# Revit family: REVIT-TR-250-3000
name_source: partatom
category: Mechanical Equipment
revit_build: Autodesk Revit 2017 (Build: 20190507_1515(x64)
units: mm (PartAtom-declared; Revit-internal decimal feet)

## family parameters
Always vertical = Yes
Cut with Voids When Loaded = No
Part Type = Normal
Room Calculation Point = No
Round Connector Dimension = Use Radius
Shared = No
Work Plane-Based = No

## types (14) — shared parameters
Assembly Code = D3040400
Controll Access Angle = 45.00°
Description = Storage Tanks for Hot Water
Disclaimer = This rendering is for building modeling purposes only. Submittal/catalog is still the contract document. PVI reserves the right to change design and specification without notice.
Drain Angle = 90.00°
Manufacturer = PVI Industries, LLC
Manway Access Radius = 6 1/2"
Relief NPT = 1"
Relief Radius = 1/2"
URL = www.pvi.com

## per-type parameters (varying)
- L 250A-TR: Cold Inlet Extension=24"; Cold Inlet Height=17 7/8"; Cold Inlet NPT=2"; Cold Inlet Radius=1"; Drain Extension=26 7/8"; Drain Height=3 1/2"; Drain NPT=1"; Drain Radius=1/2"; Flat Side Distance=45 255/256"; From Heater Extension=24"; From Heater Height=19"; From Heater NPT=2"; From Heater Radius=1"; Gallons Storage=250 CF; Height to Upper Drain=25 9/64"; Hot Outlet NPT=2"; Hot Outlet Radius=1"; Manway Access Extension=26"; Relief Angle=45.00°; Relief Extension=24"; Relief Height=46 1/4"; Skid Length=46"; Skid Spacing=27"; SkidWidthBetweenCenters=31"; To Heater Extension=24"; To Heater Height=27"; To Heater NPT=2"; To Heater Radius=1"; Unit Diameter=46"; Unit Height=63"; Unit Radius=23"; Weight=945
- L 300A-TR: Cold Inlet Extension=24"; Cold Inlet Height=17 7/8"; Cold Inlet NPT=2"; Cold Inlet Radius=1"; Drain Extension=26 7/8"; Drain Height=3 1/2"; Drain NPT=1"; Drain Radius=1/2"; Flat Side Distance=45 255/256"; From Heater Extension=24"; From Heater Height=19"; From Heater NPT=2"; From Heater Radius=1"; Gallons Storage=300 CF; Height to Upper Drain=25 9/64"; Hot Outlet NPT=2"; Hot Outlet Radius=1"; Manway Access Extension=26"; Relief Angle=45.00°; Relief Extension=24"; Relief Height=58 1/4"; Skid Length=46"; Skid Spacing=27"; SkidWidthBetweenCenters=31"; To Heater Extension=24"; To Heater Height=27"; To Heater NPT=2"; To Heater Radius=1"; Unit Diameter=46"; Unit Height=75"; Unit Radius=23"; Weight=1010
- L 400A-TR: Cold Inlet Extension=24"; Cold Inlet Height=17 7/8"; Cold Inlet NPT=2"; Cold Inlet Radius=1"; Drain Extension=26 7/8"; Drain Height=3 1/2"; Drain NPT=1"; Drain Radius=1/2"; Flat Side Distance=45 255/256"; From Heater Extension=24"; From Heater Height=19"; From Heater NPT=2"; From Heater Radius=1"; Gallons Storage=400 CF; Height to Upper Drain=25 9/64"; Hot Outlet NPT=2"; Hot Outlet Radius=1"; Manway Access Extension=26"; Relief Angle=45.00°; Relief Extension=24"; Relief Height=70 1/4"; Skid Length=46"; Skid Spacing=27"; SkidWidthBetweenCenters=31"; To Heater Extension=24"; To Heater Height=27"; To Heater NPT=2"; To Heater Radius=1"; Unit Diameter=46"; Unit Height=87"; Unit Radius=23"; Weight=1070
- L 500A-TR: Cold Inlet Extension=29"; Cold Inlet Height=19 3/4"; Cold Inlet NPT=3"; Cold Inlet Radius=1 1/2"; Drain Extension=31 7/8"; Drain Height=3 3/4"; Drain NPT=1 1/2"; Drain Radius=3/4"; Flat Side Distance=55 255/256"; From Heater Extension=29"; From Heater Height=24"; From Heater NPT=3"; From Heater Radius=1 1/2"; Gallons Storage=500 CF; Height to Upper Drain=25 9/64"; Hot Outlet NPT=3"; Hot Outlet Radius=1 1/2"; Manway Access Extension=31"; Relief Angle=38.00°; Relief Extension=29"; Relief Height=59 1/2"; Skid Length=54 1/2"; Skid Spacing=27"; SkidWidthBetweenCenters=31"; To Heater Extension=29"; To Heater Height=32"; To Heater NPT=3"; To Heater Radius=1 1/2"; Unit Diameter=56"; Unit Height=78"; Unit Radius=28"; Weight=1415
- L 600A-TR: Cold Inlet Extension=29"; Cold Inlet Height=19 3/4"; Cold Inlet NPT=3"; Cold Inlet Radius=1 1/2"; Drain Extension=31 7/8"; Drain Height=3 3/4"; Drain NPT=1 1/2"; Drain Radius=3/4"; Flat Side Distance=55 255/256"; From Heater Extension=29"; From Heater Height=24"; From Heater NPT=3"; From Heater Radius=1 1/2"; Gallons Storage=600 CF; Height to Upper Drain=25 9/64"; Hot Outlet NPT=3"; Hot Outlet Radius=1 1/2"; Manway Access Extension=31"; Relief Angle=38.00°; Relief Extension=29"; Relief Height=71 1/2"; Skid Length=54 1/2"; Skid Spacing=27"; SkidWidthBetweenCenters=31"; To Heater Extension=29"; To Heater Height=32"; To Heater NPT=3"; To Heater Radius=1 1/2"; Unit Diameter=56"; Unit Height=90"; Unit Radius=28"; Weight=1605
- L 750A-TR: Cold Inlet Extension=34 1/2"; Cold Inlet Height=22 1/2"; Cold Inlet NPT=3"; Cold Inlet Radius=1 1/2"; Drain Extension=37 3/8"; Drain Height=3 3/4"; Drain NPT=1 1/2"; Drain Radius=3/4"; Flat Side Distance=66 255/256"; From Heater Extension=34 1/2"; From Heater Height=24"; From Heater NPT=3"; From Heater Radius=1 1/2"; Gallons Storage=750 CF; Height to Upper Drain=25 9/64"; Hot Outlet NPT=3"; Hot Outlet Radius=1 1/2"; Manway Access Extension=36 1/2"; Relief Angle=45.00°; Relief Extension=34 1/2"; Relief Height=62 1/4"; Skid Length=68"; Skid Spacing=36"; SkidWidthBetweenCenters=40"; To Heater Extension=34 1/2"; To Heater Height=32"; To Heater NPT=3"; To Heater Radius=1 1/2"; Unit Diameter=67"; Unit Height=83"; Unit Radius=33 1/2"; Weight=1770
- L 900A-TR: Cold Inlet Extension=34 1/2"; Cold Inlet Height=22 1/2"; Cold Inlet NPT=3"; Cold Inlet Radius=1 1/2"; Drain Extension=37 3/8"; Drain Height=3 3/4"; Drain NPT=1 1/2"; Drain Radius=3/4"; Flat Side Distance=66 255/256"; From Heater Extension=34 1/2"; From Heater Height=24"; From Heater NPT=3"; From Heater Radius=1 1/2"; Gallons Storage=900 CF; Height to Upper Drain=25 9/64"; Hot Outlet NPT=3"; Hot Outlet Radius=1 1/2"; Manway Access Extension=36 1/2"; Relief Angle=45.00°; Relief Extension=34 1/2"; Relief Height=74 1/4"; Skid Length=68"; Skid Spacing=36"; SkidWidthBetweenCenters=40"; To Heater Extension=34 1/2"; To Heater Height=32"; To Heater NPT=3"; To Heater Radius=1 1/2"; Unit Diameter=67"; Unit Height=95"; Unit Radius=33 1/2"; Weight=1990
- L 1000A-TR: Cold Inlet Extension=34 1/2"; Cold Inlet Height=22 1/2"; Cold Inlet NPT=3"; Cold Inlet Radius=1 1/2"; Drain Extension=37 3/8"; Drain Height=3 3/4"; Drain NPT=1 1/2"; Drain Radius=3/4"; Flat Side Distance=66 255/256"; From Heater Extension=34 1/2"; From Heater Height=24"; From Heater NPT=3"; From Heater Radius=1 1/2"; Gallons Storage=1000 CF; Height to Upper Drain=25 9/64"; Hot Outlet NPT=3"; Hot Outlet Radius=1 1/2"; Manway Access Extension=36 1/2"; Relief Angle=45.00°; Relief Extension=34 1/2"; Relief Height=86 1/4"; Skid Length=68"; Skid Spacing=36"; SkidWidthBetweenCenters=40"; To Heater Extension=34 1/2"; To Heater Height=32"; To Heater NPT=3"; To Heater Radius=1 1/2"; Unit Diameter=67"; Unit Height=107"; Unit Radius=33 1/2"; Weight=2210
- L 1250A-TR: Cold Inlet Extension=38 1/2"; Cold Inlet Height=22 1/2"; Cold Inlet NPT=3"; Cold Inlet Radius=1 1/2"; Drain Extension=41 3/8"; Drain Height=3 3/4"; Drain NPT=1 1/2"; Drain Radius=3/4"; Flat Side Distance=74 255/256"; From Heater Extension=38 1/2"; From Heater Height=23"; From Heater NPT=3"; From Heater Radius=1 1/2"; Gallons Storage=1250 CF; Height to Upper Drain=25"; Hot Outlet NPT=3"; Hot Outlet Radius=1 1/2"; Manway Access Extension=40 1/2"; Relief Angle=67.50°; Relief Extension=38 1/2"; Relief Height=76 1/4"; Skid Length=75"; Skid Spacing=43"; SkidWidthBetweenCenters=47"; To Heater Extension=38 1/2"; To Heater Height=31"; To Heater NPT=3"; To Heater Radius=1 1/2"; Unit Diameter=75"; Unit Height=96"; Unit Radius=37 1/2"; Weight=3030
- L 1500A-TR: Cold Inlet Extension=38 1/2"; Cold Inlet Height=22 1/2"; Cold Inlet NPT=3"; Cold Inlet Radius=1 1/2"; Drain Extension=41 3/8"; Drain Height=3 3/4"; Drain NPT=1 1/2"; Drain Radius=3/4"; Flat Side Distance=74 255/256"; From Heater Extension=38 1/2"; From Heater Height=23"; From Heater NPT=3"; From Heater Radius=1 1/2"; Gallons Storage=1500 CF; Height to Upper Drain=22"; Hot Outlet NPT=3"; Hot Outlet Radius=1 1/2"; Manway Access Extension=40 1/2"; Relief Angle=67.50°; Relief Extension=38 1/2"; Relief Height=85 1/4"; Skid Length=75"; Skid Spacing=43"; SkidWidthBetweenCenters=47"; To Heater Extension=38 1/2"; To Heater Height=31"; To Heater NPT=3"; To Heater Radius=1 1/2"; Unit Diameter=75"; Unit Height=108"; Unit Radius=37 1/2"; Weight=3245
- L 1750A-TR: Cold Inlet Extension=38 1/2"; Cold Inlet Height=22 1/2"; Cold Inlet NPT=3"; Cold Inlet Radius=1 1/2"; Drain Extension=41 3/8"; Drain Height=3 3/4"; Drain NPT=1 1/2"; Drain Radius=3/4"; Flat Side Distance=74 255/256"; From Heater Extension=38 1/2"; From Heater Height=23"; From Heater NPT=3"; From Heater Radius=1 1/2"; Gallons Storage=1750 CF; Height to Upper Drain=22"; Hot Outlet NPT=3"; Hot Outlet Radius=1 1/2"; Manway Access Extension=40 1/2"; Relief Angle=67.50°; Relief Extension=38 1/2"; Relief Height=109 1/4"; Skid Length=75"; Skid Spacing=43"; SkidWidthBetweenCenters=47"; To Heater Extension=38 1/2"; To Heater Height=31"; To Heater NPT=3"; To Heater Radius=1 1/2"; Unit Diameter=75"; Unit Height=130"; Unit Radius=37 1/2"; Weight=3685
- L 2000A-TR: Cold Inlet Extension=38 1/2"; Cold Inlet Height=22 1/2"; Cold Inlet NPT=3"; Cold Inlet Radius=1 1/2"; Drain Extension=41 3/8"; Drain Height=3 3/4"; Drain NPT=2"; Drain Radius=1"; Flat Side Distance=74 255/256"; From Heater Extension=38 1/2"; From Heater Height=23"; From Heater NPT=3"; From Heater Radius=1 1/2"; Gallons Storage=2000 CF; Height to Upper Drain=25 9/64"; Hot Outlet NPT=3"; Hot Outlet Radius=1 1/2"; Manway Access Extension=40 1/2"; Relief Angle=67.50°; Relief Extension=38 1/2"; Relief Height=121 1/4"; Skid Length=75"; Skid Spacing=43"; SkidWidthBetweenCenters=47"; To Heater Extension=38 1/2"; To Heater Height=31"; To Heater NPT=3"; To Heater Radius=1 1/2"; Unit Diameter=75"; Unit Height=144"; Unit Radius=37 1/2"; Weight=4160
- L 2500A-TR: Cold Inlet Extension=38 1/2"; Cold Inlet Height=22 1/2"; Cold Inlet NPT=3"; Cold Inlet Radius=1 1/2"; Drain Extension=41 3/8"; Drain Height=3 3/4"; Drain NPT=2"; Drain Radius=1"; Flat Side Distance=74 255/256"; From Heater Extension=38 1/2"; From Heater Height=23"; From Heater NPT=3"; From Heater Radius=1 1/2"; Gallons Storage=2500 CF; Height to Upper Drain=25 9/64"; Hot Outlet NPT=3"; Hot Outlet Radius=1 1/2"; Manway Access Extension=40 1/2"; Relief Angle=67.50°; Relief Extension=38 1/2"; Relief Height=133 1/4"; Skid Length=75"; Skid Spacing=43"; SkidWidthBetweenCenters=47"; To Heater Extension=38 1/2"; To Heater Height=31"; To Heater NPT=3"; To Heater Radius=1 1/2"; Unit Diameter=75"; Unit Height=156"; Unit Radius=37 1/2"; Weight=4425
- L 3000A-TR: Cold Inlet Extension=38 1/2"; Cold Inlet Height=22 1/2"; Cold Inlet NPT=3"; Cold Inlet Radius=1 1/2"; Drain Extension=41 3/8"; Drain Height=3 3/4"; Drain NPT=2"; Drain Radius=1"; Flat Side Distance=74 255/256"; From Heater Extension=38 1/2"; From Heater Height=23"; From Heater NPT=3"; From Heater Radius=1 1/2"; Gallons Storage=3000 CF; Height to Upper Drain=25 9/64"; Hot Outlet NPT=3"; Hot Outlet Radius=1 1/2"; Manway Access Extension=40 1/2"; Relief Angle=67.50°; Relief Extension=38 1/2"; Relief Height=157 1/4"; Skid Length=75"; Skid Spacing=43"; SkidWidthBetweenCenters=47"; To Heater Extension=38 1/2"; To Heater Height=31"; To Heater NPT=3"; To Heater Radius=1 1/2"; Unit Diameter=75"; Unit Height=180"; Unit Radius=37 1/2"; Weight=4865

note: column(s) folded — value = type name in every type: Model

## geometry (parser evidence)
native form markers: Sweep x2
no freeform markers — native parametric forms only
